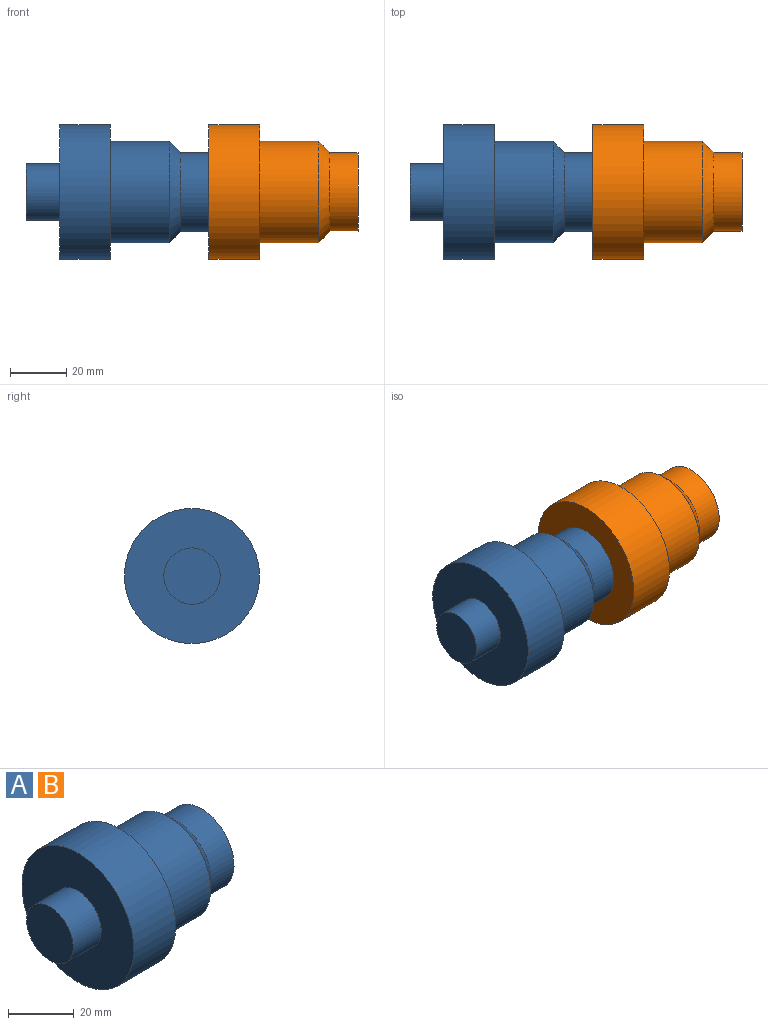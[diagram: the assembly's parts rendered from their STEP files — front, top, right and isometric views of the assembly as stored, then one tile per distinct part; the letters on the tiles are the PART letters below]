
ASSEMBLY  parts=2 mates=1
PART A: 11 faces, bbox 65x48x48 mm
  f0: plane 20x20mm, normal (-1,0,0), area 314.2mm2, adj f10
  f1: plane 20x20mm, normal (1,0,0), area 314.2mm2, adj f2
  f2: cylinder r=10mm len=30mm, axis (-1,0,0), area 1885mm2, adj f1,f3
  f3: plane 28x28mm, normal (1,0,0), area 301.6mm2, adj f2,f4
  f4: cylinder r=14mm len=28mm, axis (-1,0,0), area 879.6mm2, adj f3,f5
  f5: cone r=18mm half-angle=45deg, axis (-1,0,0), area 568.7mm2, adj f4,f6
  f6: cylinder r=18mm len=36mm, axis (-1,0,0), area 2375mm2, adj f5,f7
  f7: plane 48x48mm, normal (1,0,0), area 791.7mm2, adj f6,f8
  f8: cylinder r=24mm len=48mm, axis (-1,0,0), area 2714.3mm2, adj f7,f9
  f9: plane 48x48mm, normal (-1,0,0), area 1495.4mm2, adj f8,f10
  f10: cylinder r=10mm len=20mm, axis (-1,0,0), area 754mm2, adj f0,f9
PART B: same geometry as A
PLACE A t=(-23.96,-36.75,-11.18)mm
PLACE B t=(29.04,-36.75,-11.18)mm
MATE revolute A.f2 <-> B.f2  axis (-1,0,0) through (7.94,-36.75,-11.18)mm
